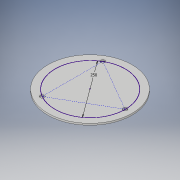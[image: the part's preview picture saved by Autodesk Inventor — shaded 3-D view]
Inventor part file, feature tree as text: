
AUTODESK INVENTOR PART (.ipt)
format: ipt  version: 2019 (Build 230136000, 136)  size: 107,008 bytes
history: native  units: in
note: dims shown in document units (in); Inventor stores cm internally (conversion verified against a paired STEP export)
features: hole x3, sketch x2, extrude x1
ambient origin geometry x8: Origin, YZ Plane, XZ Plane, XY Plane, X Axis, Y Axis, Z Axis, Center Point
bodies: Body1 (feature_tree)
feature tree (6):
  extrude  "Extrusion3"  Depth=0.2362in TaperAngle=0.0deg
  sketch  "Sketch7"  dims[d20=9.8425in d22=0.5906in d23=0.2362in d24=0.1575in d25=0.0787in d26=90.0deg d27=0.1575in d28=0.0in d29=0.5906in d30=0.2362in d31=0.1575in d32=0.0787in d33=90.0deg d34=0.1575in d35=0.0in d36=0.5906in d37=0.2362in d38=0.1575in d39=0.0787in d40=90.0deg d41=0.1575in d42=0.0in]
  hole  "Hole2"  [1 undecoded]
  hole  "Hole3"  [1 undecoded]
  hole  "Hole4"  [1 undecoded]
  sketch  "Sketch6"  dims[d17=11.811in d18=0.2362in d19=0.0in]
note: 3 required parameter values undecoded (feature->parameter linkage not recoverable at this tier; creation-order binding heuristic only, values carry confidence <= 0.55)
